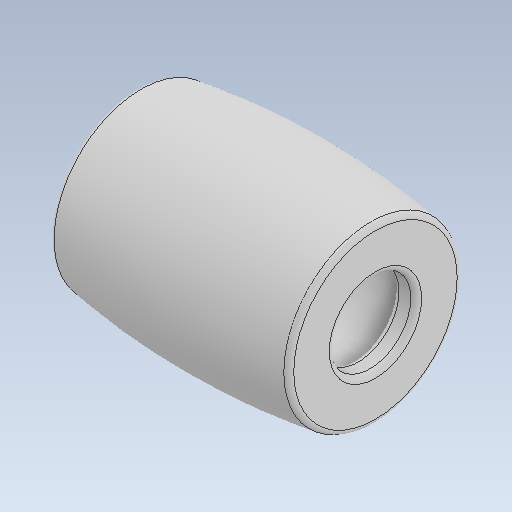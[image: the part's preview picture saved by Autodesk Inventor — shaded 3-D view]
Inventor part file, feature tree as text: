
AUTODESK INVENTOR PART (.ipt)
format: ipt  version: 2020 (Build 240168000, 168)  size: 167,936 bytes
history: native  units: in
note: dims shown in document units (in); Inventor stores cm internally (conversion verified against a paired STEP export)
features: fillet x1
ambient origin geometry x8: Origin, YZ Plane, XZ Plane, XY Plane, X Axis, Y Axis, Z Axis, Center Point
bodies: Solid1 (feature_tree)
feature tree (1):
  fillet  "Fillet2"  [1 undecoded]
note: 1 required parameter value undecoded (feature->parameter linkage not recoverable at this tier; creation-order binding heuristic only, values carry confidence <= 0.55)
